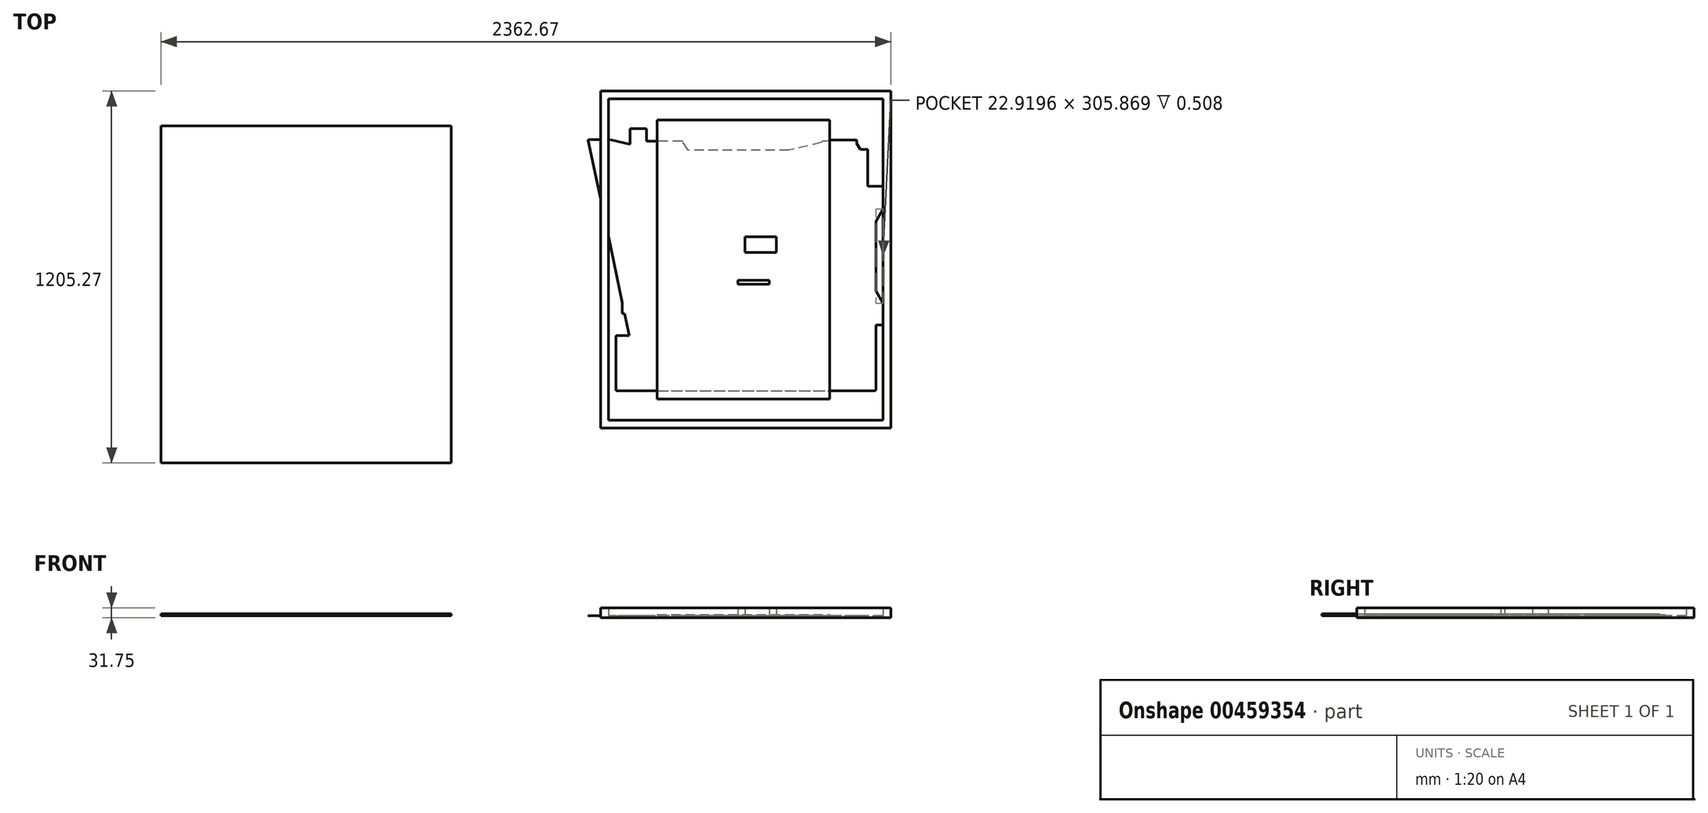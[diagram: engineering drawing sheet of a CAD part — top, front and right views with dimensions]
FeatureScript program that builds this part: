
annotation { "Feature Type Name" : "Feature", "Feature Type Description" : "" }
export const myFeature = defineFeature(function(context is Context, id is Id, definition is map)
    precondition{}
    {
        {
            var Q0;
            Q0=qCreatedBy(makeId("Top.planeOp"),FACE);
            var sketch = newSketch(context, id + "F0", { "sketchPlane" : qUnion([Q0])});
            skLineSegment(sketch, "E0", {"start": v(-243.34, 292.06) * mm, "end": v(-243.34, 202.13) * mm});
            skLineSegment(sketch, "E1", {"start": v(-243.34, 202.13) * mm, "end": v(-457.97, 202.13) * mm});
            skLineSegment(sketch, "E2", {"start": v(-457.97, 202.13) * mm, "end": v(-457.97, 99.92) * mm});
            skLineSegment(sketch, "E3", {"start": v(-457.97, 99.92) * mm, "end": v(-399.2, 99.92) * mm});
            skLineSegment(sketch, "E4", {"start": v(-399.2, 99.92) * mm, "end": v(-399.2, -176.02) * mm});
            skLineSegment(sketch, "E5", {"start": v(-399.2, -176.02) * mm, "end": v(-243.34, -176.02) * mm});
            skLineSegment(sketch, "E6", {"start": v(-243.34, -176.02) * mm, "end": v(-243.34, -268) * mm});
            skLineSegment(sketch, "E7", {"start": v(-243.34, -268) * mm, "end": v(230.62, -268) * mm});
            skLineSegment(sketch, "E8", {"start": v(230.62, -268) * mm, "end": v(230.62, -178.07) * mm});
            skLineSegment(sketch, "E9", {"start": v(230.62, -178.07) * mm, "end": v(346.88, -178.07) * mm});
            skLineSegment(sketch, "E10", {"start": v(346.88, -178.07) * mm, "end": v(381.37, -212.56) * mm});
            skLineSegment(sketch, "E11", {"start": v(381.37, -212.56) * mm, "end": v(446.53, -212.56) * mm});
            skLineSegment(sketch, "E12", {"start": v(446.53, -212.56) * mm, "end": v(446.53, -145.36) * mm});
            skLineSegment(sketch, "E13", {"start": v(446.53, -145.36) * mm, "end": v(401.81, -67.43) * mm});
            skLineSegment(sketch, "E14", {"start": v(401.81, -67.43) * mm, "end": v(401.81, 88.43) * mm});
            skLineSegment(sketch, "E15", {"start": v(401.81, 88.43) * mm, "end": v(446.53, 167.63) * mm});
            skLineSegment(sketch, "E16", {"start": v(446.53, 167.63) * mm, "end": v(446.53, 237.9) * mm});
            skLineSegment(sketch, "E17", {"start": v(446.53, 237.9) * mm, "end": v(380.1, 237.9) * mm});
            skLineSegment(sketch, "E18", {"start": v(380.1, 237.9) * mm, "end": v(346.88, 202.13) * mm});
            skLineSegment(sketch, "E19", {"start": v(346.88, 202.13) * mm, "end": v(230.62, 202.13) * mm});
            skLineSegment(sketch, "E20", {"start": v(230.62, 202.13) * mm, "end": v(230.62, 290.79) * mm});
            skLineSegment(sketch, "E21", {"start": v(230.62, 290.79) * mm, "end": v(-243.34, 292.06) * mm});
            skSolve(sketch);
        }
        {
            var Q0;
            Q0=makeQuery(id+"F0.imprint","IMPRINT",FACE,{"disambiguationData":[TD([[makeQuery(id+"F0.imprint","IMPRINT",EDGE,{"derivedFrom":sQuery(id+"F0.wireOp",EDGE,"E0")}),1.0]])]});
            extrude(context, id + "F1", {"entities" : qUnion([Q0]), "depth" : 0.5 * mm});
        }
        {
            var Q0;
            Q0=makeQuery(id+"F1.opExtrude","SWEPT_EDGE",EDGE,{"disambiguationData":[OSD([sQuery(id+"F0.wireOp",EDGE,"E0"),sQuery(id+"F0.wireOp",EDGE,"E21")])]});
            var Q1;
            Q1=makeQuery(id+"F1.opExtrude","SWEPT_EDGE",EDGE,{"disambiguationData":[OSD([sQuery(id+"F0.wireOp",EDGE,"E0"),sQuery(id+"F0.wireOp",EDGE,"E1")])]});
            var Q2;
            Q2=makeQuery(id+"F1.opExtrude","SWEPT_EDGE",EDGE,{"disambiguationData":[OSD([sQuery(id+"F0.wireOp",EDGE,"E1"),sQuery(id+"F0.wireOp",EDGE,"E2")])]});
            var Q3;
            Q3=makeQuery(id+"F1.opExtrude","SWEPT_EDGE",EDGE,{"disambiguationData":[OSD([sQuery(id+"F0.wireOp",EDGE,"E2"),sQuery(id+"F0.wireOp",EDGE,"E3")])]});
            var Q4;
            Q4=makeQuery(id+"F1.opExtrude","SWEPT_EDGE",EDGE,{"disambiguationData":[OSD([sQuery(id+"F0.wireOp",EDGE,"E3"),sQuery(id+"F0.wireOp",EDGE,"E4")])]});
            var Q5;
            Q5=makeQuery(id+"F1.opExtrude","SWEPT_EDGE",EDGE,{"disambiguationData":[OSD([sQuery(id+"F0.wireOp",EDGE,"E4"),sQuery(id+"F0.wireOp",EDGE,"E5")])]});
            var Q6;
            Q6=makeQuery(id+"F1.opExtrude","SWEPT_EDGE",EDGE,{"disambiguationData":[OSD([sQuery(id+"F0.wireOp",EDGE,"E5"),sQuery(id+"F0.wireOp",EDGE,"E6")])]});
            var Q7;
            Q7=makeQuery(id+"F1.opExtrude","SWEPT_EDGE",EDGE,{"disambiguationData":[OSD([sQuery(id+"F0.wireOp",EDGE,"E6"),sQuery(id+"F0.wireOp",EDGE,"E7")])]});
            var Q8;
            Q8=makeQuery(id+"F1.opExtrude","SWEPT_EDGE",EDGE,{"disambiguationData":[OSD([sQuery(id+"F0.wireOp",EDGE,"E7"),sQuery(id+"F0.wireOp",EDGE,"E8")])]});
            var Q9;
            Q9=makeQuery(id+"F1.opExtrude","SWEPT_EDGE",EDGE,{"disambiguationData":[OSD([sQuery(id+"F0.wireOp",EDGE,"E8"),sQuery(id+"F0.wireOp",EDGE,"E9")])]});
            var Q10;
            Q10=makeQuery(id+"F1.opExtrude","SWEPT_EDGE",EDGE,{"disambiguationData":[OSD([sQuery(id+"F0.wireOp",EDGE,"E10"),sQuery(id+"F0.wireOp",EDGE,"E11")])]});
            var Q11;
            Q11=makeQuery(id+"F1.opExtrude","SWEPT_EDGE",EDGE,{"disambiguationData":[OSD([sQuery(id+"F0.wireOp",EDGE,"E11"),sQuery(id+"F0.wireOp",EDGE,"E12")])]});
            var Q12;
            Q12=makeQuery(id+"F1.opExtrude","SWEPT_EDGE",EDGE,{"disambiguationData":[OSD([sQuery(id+"F0.wireOp",EDGE,"E16"),sQuery(id+"F0.wireOp",EDGE,"E17")])]});
            var Q13;
            Q13=makeQuery(id+"F1.opExtrude","SWEPT_EDGE",EDGE,{"disambiguationData":[OSD([sQuery(id+"F0.wireOp",EDGE,"E17"),sQuery(id+"F0.wireOp",EDGE,"E18")])]});
            var Q14;
            Q14=makeQuery(id+"F1.opExtrude","SWEPT_EDGE",EDGE,{"disambiguationData":[OSD([sQuery(id+"F0.wireOp",EDGE,"E19"),sQuery(id+"F0.wireOp",EDGE,"E20")])]});
            var Q15;
            Q15=makeQuery(id+"F1.opExtrude","SWEPT_EDGE",EDGE,{"disambiguationData":[OSD([sQuery(id+"F0.wireOp",EDGE,"E20"),sQuery(id+"F0.wireOp",EDGE,"E21")])]});
            fillet(context, id + "F2", {"entities" : qUnion([Q0, Q1, Q2, Q3, Q4, Q5, Q6, Q7, Q8, Q9, Q10, Q11, Q12, Q13, Q14, Q15]), "radius" : 2.54 * mm, "tangentPropagation" : true, "allowEdgeOverflow" : false});
        }
        {
            var Q0;
            Q0=qCreatedBy(makeId("Top.planeOp"),FACE);
            var sketch = newSketch(context, id + "F3", { "sketchPlane" : qUnion([Q0])});
            skLineSegment(sketch, "E22", {"start": v(-510.3, 388.98) * mm, "end": v(-354.87, -350.92) * mm});
            skLineSegment(sketch, "E23", {"start": v(-354.87, -350.92) * mm, "end": v(-158.24, -350.92) * mm});
            skLineSegment(sketch, "E24", {"start": v(-158.24, -350.92) * mm, "end": v(-158.24, -218.64) * mm});
            skLineSegment(sketch, "E25", {"start": v(-158.24, -218.64) * mm, "end": v(0, -218.64) * mm});
            skLineSegment(sketch, "E26", {"start": v(0, -218.64) * mm, "end": v(0, -348.84) * mm});
            skLineSegment(sketch, "E27", {"start": v(0, -348.84) * mm, "end": v(199.28, -348.84) * mm});
            skLineSegment(sketch, "E28", {"start": v(199.28, -348.84) * mm, "end": v(360.16, 387.65) * mm});
            skLineSegment(sketch, "E29", {"start": v(360.16, 387.65) * mm, "end": v(277.93, 387.65) * mm});
            skLineSegment(sketch, "E30", {"start": v(277.93, 387.65) * mm, "end": v(-77.8, 300.06) * mm});
            skLineSegment(sketch, "E31", {"start": v(-77.8, 300.06) * mm, "end": v(-433.52, 387.65) * mm});
            skLineSegment(sketch, "E32", {"start": v(-433.52, 387.65) * mm, "end": v(-510.3, 388.98) * mm});
            skSolve(sketch);
        }
        {
            var Q0;
            Q0 = qSketchRegion(id + "F3", true);
            extrude(context, id + "F4", {"entities" : qUnion([Q0]), "depth" : 0.5 * mm});
        }
        {
            var Q0;
            Q0=makeQuery(id+"F4.opExtrude","SWEPT_EDGE",EDGE,{"disambiguationData":[OSD([sQuery(id+"F3.wireOp",EDGE,"E23"),sQuery(id+"F3.wireOp",EDGE,"E24")])]});
            var Q1;
            Q1=makeQuery(id+"F4.opExtrude","SWEPT_EDGE",EDGE,{"disambiguationData":[OSD([sQuery(id+"F3.wireOp",EDGE,"E24"),sQuery(id+"F3.wireOp",EDGE,"E25")])]});
            var Q2;
            Q2=makeQuery(id+"F4.opExtrude","SWEPT_EDGE",EDGE,{"disambiguationData":[OSD([sQuery(id+"F3.wireOp",EDGE,"E25"),sQuery(id+"F3.wireOp",EDGE,"E26")])]});
            var Q3;
            Q3=makeQuery(id+"F4.opExtrude","SWEPT_EDGE",EDGE,{"disambiguationData":[OSD([sQuery(id+"F3.wireOp",EDGE,"E26"),sQuery(id+"F3.wireOp",EDGE,"E27")])]});
            var Q4;
            Q4=makeQuery(id+"F4.opExtrude","SWEPT_EDGE",EDGE,{"disambiguationData":[OSD([sQuery(id+"F3.wireOp",EDGE,"E22"),sQuery(id+"F3.wireOp",EDGE,"E23")])]});
            var Q5;
            Q5=makeQuery(id+"F4.opExtrude","SWEPT_EDGE",EDGE,{"disambiguationData":[OSD([sQuery(id+"F3.wireOp",EDGE,"E27"),sQuery(id+"F3.wireOp",EDGE,"E28")])]});
            var Q6;
            Q6=makeQuery(id+"F4.opExtrude","SWEPT_EDGE",EDGE,{"disambiguationData":[OSD([sQuery(id+"F3.wireOp",EDGE,"E28"),sQuery(id+"F3.wireOp",EDGE,"E29")])]});
            var Q7;
            Q7=makeQuery(id+"F4.opExtrude","SWEPT_EDGE",EDGE,{"disambiguationData":[OSD([sQuery(id+"F3.wireOp",EDGE,"E22"),sQuery(id+"F3.wireOp",EDGE,"E32")])]});
            fillet(context, id + "F5", {"entities" : qUnion([Q0, Q1, Q2, Q3, Q4, Q5, Q6, Q7]), "radius" : 2.54 * mm, "tangentPropagation" : true, "allowEdgeOverflow" : false});
        }
        {
            var Q0;
            Q0=makeQuery(id+"F4.opExtrude","SWEPT_EDGE",EDGE,{"disambiguationData":[OSD([sQuery(id+"F3.wireOp",EDGE,"E30"),sQuery(id+"F3.wireOp",EDGE,"E31")])]});
            fillet(context, id + "F6", {"entities" : qUnion([Q0]), "radius" : 50.8 * mm, "tangentPropagation" : true, "allowEdgeOverflow" : false});
        }
        {
            var Q0;
            Q0=qCreatedBy(makeId("Top.planeOp"),FACE);
            var sketch = newSketch(context, id + "F7", { "sketchPlane" : qUnion([Q0])});
            skLineSegment(sketch, "E33", {"start": v(-374.29, 424.37) * mm, "end": v(-374.29, 105.57) * mm});
            skLineSegment(sketch, "E34", {"start": v(-374.29, 105.57) * mm, "end": v(-420.18, 105.57) * mm});
            skLineSegment(sketch, "E35", {"start": v(-420.18, 105.57) * mm, "end": v(-420.18, -9.15) * mm});
            skLineSegment(sketch, "E36", {"start": v(-420.18, -9.15) * mm, "end": v(-374.29, -9.15) * mm});
            skLineSegment(sketch, "E37", {"start": v(-374.29, -9.15) * mm, "end": v(-374.29, -247.2) * mm});
            skLineSegment(sketch, "E38", {"start": v(-374.29, -247.2) * mm, "end": v(-420.18, -247.2) * mm});
            skLineSegment(sketch, "E39", {"start": v(-420.18, -247.2) * mm, "end": v(-420.18, -425.01) * mm});
            skLineSegment(sketch, "E40", {"start": v(-420.18, -425.01) * mm, "end": v(421.58, -425.01) * mm});
            skLineSegment(sketch, "E41", {"start": v(421.58, -425.01) * mm, "end": v(421.58, 164.36) * mm});
            skLineSegment(sketch, "E42", {"start": v(421.58, 164.36) * mm, "end": v(395.77, 188.74) * mm});
            skLineSegment(sketch, "E43", {"start": v(395.77, 188.74) * mm, "end": v(395.77, 356.52) * mm});
            skLineSegment(sketch, "E44", {"start": v(395.77, 356.52) * mm, "end": v(371.4, 356.52) * mm});
            skLineSegment(sketch, "E45", {"start": v(371.4, 356.52) * mm, "end": v(354.18, 383.76) * mm});
            skLineSegment(sketch, "E46", {"start": v(354.18, 383.76) * mm, "end": v(248.07, 383.76) * mm});
            skLineSegment(sketch, "E47", {"start": v(248.07, 383.76) * mm, "end": v(229.42, 353.65) * mm});
            skLineSegment(sketch, "E48", {"start": v(229.42, 353.65) * mm, "end": v(-186.43, 353.65) * mm});
            skLineSegment(sketch, "E49", {"start": v(-186.43, 353.65) * mm, "end": v(-205.08, 383.76) * mm});
            skLineSegment(sketch, "E50", {"start": v(-205.08, 383.76) * mm, "end": v(-321.23, 383.76) * mm});
            skLineSegment(sketch, "E51", {"start": v(-321.23, 383.76) * mm, "end": v(-321.23, 424.37) * mm});
            skLineSegment(sketch, "E52", {"start": v(-321.23, 424.37) * mm, "end": v(-374.29, 424.37) * mm});
            skSolve(sketch);
        }
        {
            var Q0;
            Q0=makeQuery(id+"F7.imprint","IMPRINT",FACE,{"disambiguationData":[TD([[makeQuery(id+"F7.imprint","IMPRINT",EDGE,{"derivedFrom":sQuery(id+"F7.wireOp",EDGE,"E33")}),1.0]])]});
            extrude(context, id + "F8", {"entities" : qUnion([Q0]), "depth" : 0.5 * mm});
        }
        {
            var Q0;
            Q0=makeQuery(id+"F8.opExtrude","SWEPT_EDGE",EDGE,{"disambiguationData":[OSD([sQuery(id+"F7.wireOp",EDGE,"E33"),sQuery(id+"F7.wireOp",EDGE,"E52")])]});
            var Q1;
            Q1=makeQuery(id+"F8.opExtrude","SWEPT_EDGE",EDGE,{"disambiguationData":[OSD([sQuery(id+"F7.wireOp",EDGE,"E33"),sQuery(id+"F7.wireOp",EDGE,"E34")])]});
            var Q2;
            Q2=makeQuery(id+"F8.opExtrude","SWEPT_EDGE",EDGE,{"disambiguationData":[OSD([sQuery(id+"F7.wireOp",EDGE,"E34"),sQuery(id+"F7.wireOp",EDGE,"E35")])]});
            var Q3;
            Q3=makeQuery(id+"F8.opExtrude","SWEPT_EDGE",EDGE,{"disambiguationData":[OSD([sQuery(id+"F7.wireOp",EDGE,"E35"),sQuery(id+"F7.wireOp",EDGE,"E36")])]});
            var Q4;
            Q4=makeQuery(id+"F8.opExtrude","SWEPT_EDGE",EDGE,{"disambiguationData":[OSD([sQuery(id+"F7.wireOp",EDGE,"E36"),sQuery(id+"F7.wireOp",EDGE,"E37")])]});
            var Q5;
            Q5=makeQuery(id+"F8.opExtrude","SWEPT_EDGE",EDGE,{"disambiguationData":[OSD([sQuery(id+"F7.wireOp",EDGE,"E37"),sQuery(id+"F7.wireOp",EDGE,"E38")])]});
            var Q6;
            Q6=makeQuery(id+"F8.opExtrude","SWEPT_EDGE",EDGE,{"disambiguationData":[OSD([sQuery(id+"F7.wireOp",EDGE,"E38"),sQuery(id+"F7.wireOp",EDGE,"E39")])]});
            var Q7;
            Q7=makeQuery(id+"F8.opExtrude","SWEPT_EDGE",EDGE,{"disambiguationData":[OSD([sQuery(id+"F7.wireOp",EDGE,"E39"),sQuery(id+"F7.wireOp",EDGE,"E40")])]});
            var Q8;
            Q8=makeQuery(id+"F8.opExtrude","SWEPT_EDGE",EDGE,{"disambiguationData":[OSD([sQuery(id+"F7.wireOp",EDGE,"E40"),sQuery(id+"F7.wireOp",EDGE,"E41")])]});
            var Q9;
            Q9=makeQuery(id+"F8.opExtrude","SWEPT_EDGE",EDGE,{"disambiguationData":[OSD([sQuery(id+"F7.wireOp",EDGE,"E43"),sQuery(id+"F7.wireOp",EDGE,"E44")])]});
            var Q10;
            Q10=makeQuery(id+"F8.opExtrude","SWEPT_EDGE",EDGE,{"disambiguationData":[OSD([sQuery(id+"F7.wireOp",EDGE,"E45"),sQuery(id+"F7.wireOp",EDGE,"E46")])]});
            var Q11;
            Q11=makeQuery(id+"F8.opExtrude","SWEPT_EDGE",EDGE,{"disambiguationData":[OSD([sQuery(id+"F7.wireOp",EDGE,"E46"),sQuery(id+"F7.wireOp",EDGE,"E47")])]});
            var Q12;
            Q12=makeQuery(id+"F8.opExtrude","SWEPT_EDGE",EDGE,{"disambiguationData":[OSD([sQuery(id+"F7.wireOp",EDGE,"E49"),sQuery(id+"F7.wireOp",EDGE,"E50")])]});
            var Q13;
            Q13=makeQuery(id+"F8.opExtrude","SWEPT_EDGE",EDGE,{"disambiguationData":[OSD([sQuery(id+"F7.wireOp",EDGE,"E50"),sQuery(id+"F7.wireOp",EDGE,"E51")])]});
            var Q14;
            Q14=makeQuery(id+"F8.opExtrude","SWEPT_EDGE",EDGE,{"disambiguationData":[OSD([sQuery(id+"F7.wireOp",EDGE,"E51"),sQuery(id+"F7.wireOp",EDGE,"E52")])]});
            fillet(context, id + "F9", {"entities" : qUnion([Q0, Q1, Q2, Q3, Q4, Q5, Q6, Q7, Q8, Q9, Q10, Q11, Q12, Q13, Q14]), "radius" : 2.54 * mm, "tangentPropagation" : true, "allowEdgeOverflow" : false});
        }
        {
            var Q0;
            Q0=qCreatedBy(makeId("Top.planeOp"),FACE);
            var sketch = newSketch(context, id + "F10", { "sketchPlane" : qUnion([Q0])});
            skLineSegment(sketch, "E53.bottom", {"start": v(444.5, 520.7) * mm, "end": v(-444.5, 520.7) * mm});
            skLineSegment(sketch, "E53.top", {"start": v(444.5, -520.7) * mm, "end": v(-444.5, -520.7) * mm});
            skLineSegment(sketch, "E53.left", {"start": v(444.5, 520.7) * mm, "end": v(444.5, -520.7) * mm});
            skLineSegment(sketch, "E53.right", {"start": v(-444.5, 520.7) * mm, "end": v(-444.5, -520.7) * mm});
            skPoint(sketch, "E53.middle", {"position": v(0, 0) * mm});
            skLineSegment(sketch, "E54.bottom", {"start": v(469.9, 546.1) * mm, "end": v(-469.9, 546.1) * mm});
            skLineSegment(sketch, "E54.top", {"start": v(469.9, -546.1) * mm, "end": v(-469.9, -546.1) * mm});
            skLineSegment(sketch, "E54.left", {"start": v(469.9, 546.1) * mm, "end": v(469.9, -546.1) * mm});
            skLineSegment(sketch, "E54.right", {"start": v(-469.9, 546.1) * mm, "end": v(-469.9, -546.1) * mm});
            skSolve(sketch);
        }
        {
            var Q0;
            Q0=makeQuery(id+"F10.imprint","IMPRINT",FACE,{"disambiguationData":[TD([[makeQuery(id+"F10.imprint","IMPRINT",EDGE,{"derivedFrom":sQuery(id+"F10.wireOp",EDGE,"E53.bottom")}),-1.0]])]});
            extrude(context, id + "F11", {"entities" : qUnion([Q0]), "depth" : 25.4 * mm});
        }
        {
            var Q0;
            Q0=makeQuery(id+"F10.imprint","IMPRINT",FACE,{"disambiguationData":[TD([[makeQuery(id+"F10.imprint","IMPRINT",EDGE,{"derivedFrom":sQuery(id+"F10.wireOp",EDGE,"E53.bottom")}),1.0]])]});
            var Q1;
            Q1=makeQuery(id+"F10.imprint","IMPRINT",FACE,{"disambiguationData":[TD([[makeQuery(id+"F10.imprint","IMPRINT",EDGE,{"derivedFrom":sQuery(id+"F10.wireOp",EDGE,"E53.bottom")}),-1.0]])]});
            extrude(context, id + "F12", {"entities" : qUnion([Q0, Q1]), "operationType" : NewBodyOperationType.ADD, "oppositeDirection" : true, "depth" : 6.35 * mm});
        }
        {
            var Q0;
            Q0=qCreatedBy(makeId("Top.planeOp"),FACE);
            var sketch = newSketch(context, id + "F13", { "sketchPlane" : qUnion([Q0])});
            skLineSegment(sketch, "E55.bottom", {"start": v(469.9, 495.3) * mm, "end": v(-469.9, 495.3) * mm});
            skLineSegment(sketch, "E55.top", {"start": v(469.9, -495.3) * mm, "end": v(-469.9, -495.3) * mm});
            skLineSegment(sketch, "E55.left", {"start": v(469.9, 495.3) * mm, "end": v(469.9, -495.3) * mm});
            skLineSegment(sketch, "E55.right", {"start": v(-469.9, 495.3) * mm, "end": v(-469.9, -495.3) * mm});
            skPoint(sketch, "E55.middle", {"position": v(0, 0) * mm});
            skSolve(sketch);
        }
        {
            var Q0;
            Q0=qCreatedBy(makeId("Top.planeOp"),FACE);
            var sketch = newSketch(context, id + "F14", { "sketchPlane" : qUnion([Q0])});
            skLineSegment(sketch, "E56.bottom", {"start": v(528.17, 560.64) * mm, "end": v(-528.17, 560.64) * mm});
            skLineSegment(sketch, "E56.top", {"start": v(528.17, -560.64) * mm, "end": v(-528.17, -560.64) * mm});
            skLineSegment(sketch, "E56.left", {"start": v(528.17, 560.64) * mm, "end": v(528.17, -560.64) * mm});
            skLineSegment(sketch, "E56.right", {"start": v(-528.17, 560.64) * mm, "end": v(-528.17, -560.64) * mm});
            skPoint(sketch, "E56.middle", {"position": v(0, 0) * mm});
            skSolve(sketch);
        }
        {
            var Q0;
            Q0=qCreatedBy(makeId("Top.planeOp"),FACE);
            var sketch = newSketch(context, id + "F15", { "sketchPlane" : qUnion([Q0])});
            skLineSegment(sketch, "E57.bottom", {"start": v(-2.32, 22.73) * mm, "end": v(99.28, 22.73) * mm});
            skLineSegment(sketch, "E57.top", {"start": v(-2.32, 73.53) * mm, "end": v(99.28, 73.53) * mm});
            skLineSegment(sketch, "E57.left", {"start": v(-2.32, 22.73) * mm, "end": v(-2.32, 73.53) * mm});
            skLineSegment(sketch, "E57.right", {"start": v(99.28, 22.73) * mm, "end": v(99.28, 73.53) * mm});
            skSolve(sketch);
        }
        {
            var Q0;
            Q0 = qSketchRegion(id + "F15", true);
            extrude(context, id + "F16", {"entities" : qUnion([Q0]), "depth" : 25.4 * mm});
        }
        {
            var Q0;
            Q0=qCreatedBy(makeId("Top.planeOp"),FACE);
            var sketch = newSketch(context, id + "F17", { "sketchPlane" : qUnion([Q0])});
            skLineSegment(sketch, "E58.bottom", {"start": v(-25.72, -67.35) * mm, "end": v(75.88, -67.35) * mm});
            skLineSegment(sketch, "E58.top", {"start": v(-25.72, -80.05) * mm, "end": v(75.88, -80.05) * mm});
            skLineSegment(sketch, "E58.left", {"start": v(-25.72, -67.35) * mm, "end": v(-25.72, -80.05) * mm});
            skLineSegment(sketch, "E58.right", {"start": v(75.88, -67.35) * mm, "end": v(75.88, -80.05) * mm});
            skSolve(sketch);
        }
        {
            var Q0;
            Q0 = qSketchRegion(id + "F17", true);
            extrude(context, id + "F18", {"entities" : qUnion([Q0]), "depth" : 25.4 * mm});
        }
        {
            var Q0;
            Q0=qCreatedBy(makeId("Top.planeOp"),FACE);
            var sketch = newSketch(context, id + "F19", { "sketchPlane" : qUnion([Q0])});
            skLineSegment(sketch, "E59.bottom", {"start": v(-286.67, -452.7) * mm, "end": v(272.13, -452.7) * mm});
            skLineSegment(sketch, "E59.top", {"start": v(-286.67, 451.8) * mm, "end": v(272.13, 451.8) * mm});
            skLineSegment(sketch, "E59.left", {"start": v(-286.67, -452.7) * mm, "end": v(-286.67, 451.8) * mm});
            skLineSegment(sketch, "E59.right", {"start": v(272.13, -452.7) * mm, "end": v(272.13, 451.8) * mm});
            skSolve(sketch);
        }
        {
            var Q0;
            Q0=makeQuery(id+"F19.imprint","IMPRINT",FACE,{"disambiguationData":[TD([[makeQuery(id+"F19.imprint","IMPRINT",EDGE,{"derivedFrom":sQuery(id+"F19.wireOp",EDGE,"E59.bottom")}),1.0]])]});
            extrude(context, id + "F20", {"entities" : qUnion([Q0]), "depth" : 0.5 * mm});
        }
        {
            var Q0;
            Q0 = qSketchRegion(id + "F19", true);
            extrude(context, id + "F21", {"entities" : qUnion([Q0]), "depth" : 2.54 * mm});
        }
        {
            var Q0;
            Q0 = qSketchRegion(id + "F19", true);
            extrude(context, id + "F22", {"entities" : qUnion([Q0]), "depth" : 3.17 * mm});
        }
        {
            var Q0;
            Q0 = qSketchRegion(id + "F19", true);
            extrude(context, id + "F23", {"entities" : qUnion([Q0]), "depth" : 2.54 * mm});
        }
        {
            var Q0;
            Q0=qCreatedBy(makeId("Top.planeOp"),FACE);
            var sketch = newSketch(context, id + "F24", { "sketchPlane" : qUnion([Q0])});
            skLineSegment(sketch, "E60.bottom", {"start": v(-1892.77, -659.17) * mm, "end": v(-952.97, -659.17) * mm});
            skLineSegment(sketch, "E60.top", {"start": v(-1892.77, 433.03) * mm, "end": v(-952.97, 433.03) * mm});
            skLineSegment(sketch, "E60.left", {"start": v(-1892.77, -659.17) * mm, "end": v(-1892.77, 433.03) * mm});
            skLineSegment(sketch, "E60.right", {"start": v(-952.97, -659.17) * mm, "end": v(-952.97, 433.03) * mm});
            skSolve(sketch);
        }
        {
            var Q0;
            Q0 = qSketchRegion(id + "F24", true);
            extrude(context, id + "F25", {"entities" : qUnion([Q0]), "depth" : 6.35 * mm});
        }
    });
